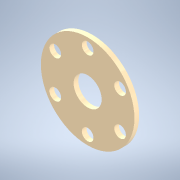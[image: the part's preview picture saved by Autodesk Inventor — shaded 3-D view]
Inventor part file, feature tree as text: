
AUTODESK INVENTOR PART (.ipt)
format: ipt  version: 2020 (Build 240168000, 168)  size: 131,072 bytes
history: native  units: mm
features: sketch x2, revolve x1, hole x1, pattern_circular x1
ambient origin geometry x8: Origin, YZ Plane, XZ Plane, XY Plane, X Axis, Y Axis, Z Axis, Center Point
bodies: Solid1 (feature_tree)
feature tree (5):
  revolve  "Revolution1"  [1 undecoded]
  hole  "Hole1"  [1 undecoded]
  pattern_circular  "Circular Pattern1"  Count=6 Angle=360.0deg
  sketch  "Sketch1"  dims[d3=2.0mm d4=40.0mm]
  sketch  "Sketch2"  dims[d5=90.0deg d6=16.0mm d7=5.0mm d8=6.0mm d9=4.0mm d10=2.0mm d11=90.0deg d12=8.0mm d13=20.594885mm d14=60.0mm d15=360.0deg d28=16.0mm]
note: 2 required parameter values undecoded (feature->parameter linkage not recoverable at this tier; creation-order binding heuristic only, values carry confidence <= 0.55)